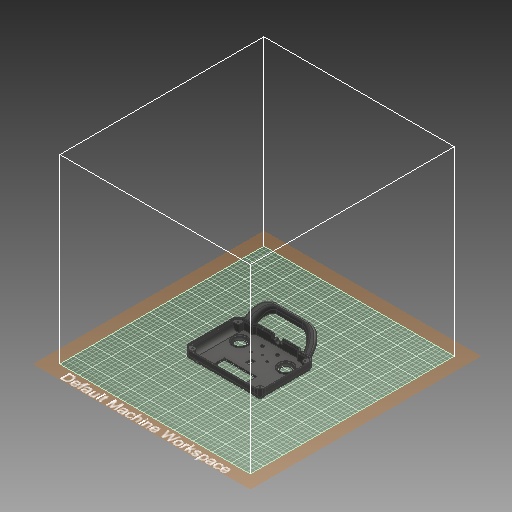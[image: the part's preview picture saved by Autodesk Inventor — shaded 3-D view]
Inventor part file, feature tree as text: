
AUTODESK INVENTOR PART (.ipt)
format: ipt  version: 2019.4 (Build 234330000, 330)  size: 1,773,568 bytes
history: native  units: in
note: dims shown in document units (in); Inventor stores cm internally (conversion verified against a paired STEP export)
features: sketch x16, move_body x13, extrude x12, fillet x11, direct_edit x7, imported_body x1
ambient origin geometry x8: Origin, YZ Plane, XZ Plane, XY Plane, X Axis, Y Axis, Z Axis, Center Point
bodies: Solid1 (feature_tree)
feature tree (60):
  imported_body  "Base1"
  fillet  "Fillet1"  Radius=0.4724in
  fillet  "Fillet2"  Radius=0.1969in
  fillet  "Fillet3"  Radius=0.1969in
  direct_edit  "Direct Edit1"
  extrude  "Extrusion1"  Depth=0.0787in TaperAngle=0.0deg
  fillet  "Fillet4"  Radius=0.1575in
  extrude  "Extrusion3"  Depth=0.3937in
  extrude  "Extrusion4"  Depth=0.2362in
  sketch  "Sketch5"  dims[d12=-0.0394in d13=0.0in d14=0.0in d16=0.1575in d17=0.0in]
  sketch  "Sketch6"  dims[d18=0.3937in d25=0.0079in]
  extrude  "Extrusion5"  Depth=0.0157in
  extrude  "Extrusion6"  Depth=0.0079in
  extrude  "Extrusion7"  Depth=0.0157in
  extrude  "Extrusion8"  TaperAngle=90.0deg  [1 undecoded]
  sketch  "Sketch11"  dims[d34=0.0079in d35=90.0deg d36=0.2362in d37=0.0157in d38=0.0157in d39=0.0157in d40=0.0157in d41=0.0157in]
  fillet  "Fillet6"  Radius=0.2362in
  fillet  "Fillet7"  Radius=0.0157in
  fillet  "Fillet8"  Radius=0.0157in
  fillet  "Fillet9"  Radius=0.0157in
  fillet  "Fillet10"  Radius=0.0157in
  fillet  "Fillet11"  Radius=0.0157in
  direct_edit  "Direct Edit2"
  direct_edit  "Direct Edit3"
  extrude  "Extrusion10"  Depth=0.0157in
  direct_edit  "Direct Edit4"
  sketch  "Sketch14"  dims[d44=0.0157in d45=0.0157in d46=0.0in]
  extrude  "Extrusion11"  Depth=0.0157in TaperAngle=0.0deg
  sketch  "Sketch16"  dims[d49=0.2362in d50=0.0157in]
  extrude  "Extrusion12"  Depth=0.0157in
  direct_edit  "Direct Edit5"
  direct_edit  "Direct Edit6"
  direct_edit  "Direct Edit7"
  extrude  "Extrusion13"  Depth=0.0157in
  extrude  "Extrusion14"  Depth=0.0079in
  fillet  "Fillet12"  [1 undecoded]
  sketch  "Sketch1"  dims[d3=0.0in d4=0.0787in d5=0.0in d6=0.0in d7=0.0394in d8=0.0in]
  sketch  "Sketch3"  dims[d9=0.0394in d10=0.0in d11=0.0in]
  sketch  "Sketch7"  dims[d26=0.0157in d27=0.2362in]
  sketch  "Sketch8"  dims[d28=0.0079in d29=0.0157in]
  sketch  "Sketch9"  dims[d30=0.2362in d31=0.0079in]
  sketch  "Sketch10"  dims[d32=0.2362in d33=0.0157in]
  sketch  "Sketch13"  dims[d42=0.0157in d43=0.0157in]
  sketch  "Sketch15"  dims[d47=0.0079in d48=0.0157in]
  sketch  "Sketch17"  dims[d51=0.0157in d52=0.0079in d53=90.0deg]
  sketch  "Sketch18"  dims[d54=0.2362in]
  sketch  "Sketch19"  dims[d55=0.0157in d56=0.0157in d57=0.0157in d58=0.0079in d59=90.0deg d60=0.2362in d61=0.0157in d62=0.0157in d63=0.0157in d64=0.0079in d65=0.0in d66=0.0157in d67=0.2362in d68=0.0157in d69=0.0157in d70=0.0in d71=1.5748in d72=0.0in d73=1.9685in d75=1.9685in d76=45.0deg d77=0.7818in d78=0.0in d79=0.7818in d80=0.0in d81=0.3937in d82=4.252in d83=0.0in d84=1.0236in d85=1.378in d86=0.3937in d87=0.3937in d88=0.1181in d89=0.0787in d102=0.0787in d103=0.0in d104=0.0in d105=-0.0394in d106=0.0in d107=0.0in d108=0.315in d109=0.1575in d110=0.5512in d111=0.0in d113=0.0in d114=0.0in d115=-0.0394in d116=0.1181in d117=0.1181in d118=0.1181in d119=0.1181in d120=0.5512in d121=0.0in d122=-0.0787in d123=0.0in d124=0.0in d125=0.0in d126=360.0deg d127=0.1575in d128=0.0in d129=0.0in d130=0.1575in d131=0.0394in d132=0.0in d133=0.0in d134=0.0787in d135=0.0039in d136=2.8031in d137=1.0157in d138=0.3937in d139=0.0in d140=0.0in d141=0.0in d142=-0.0079in d143=0.0in d144=0.0in d145=-0.0059in d146=0.0in d147=0.0in d148=-0.0059in d149=0.8858in d150=0.4724in d151=0.4331in d152=0.2756in d153=0.7874in d154=0.0in d155=1.2598in d156=1.2598in d157=0.1181in d158=0.0in d159=0.0787in]
  move_body  "Move1"
  move_body  "Move2"
  move_body  "Move3"
  move_body  "Move4"
  move_body  "Move5"
  move_body  "Move6"
  move_body  "Move7"
  move_body  "Move8"
  move_body  "Move9"
  move_body  "Move10"
  move_body  "Move11"
  move_body  "Move12"
  move_body  "Move13"
note: 2 required parameter values undecoded (feature->parameter linkage not recoverable at this tier; creation-order binding heuristic only, values carry confidence <= 0.55)
